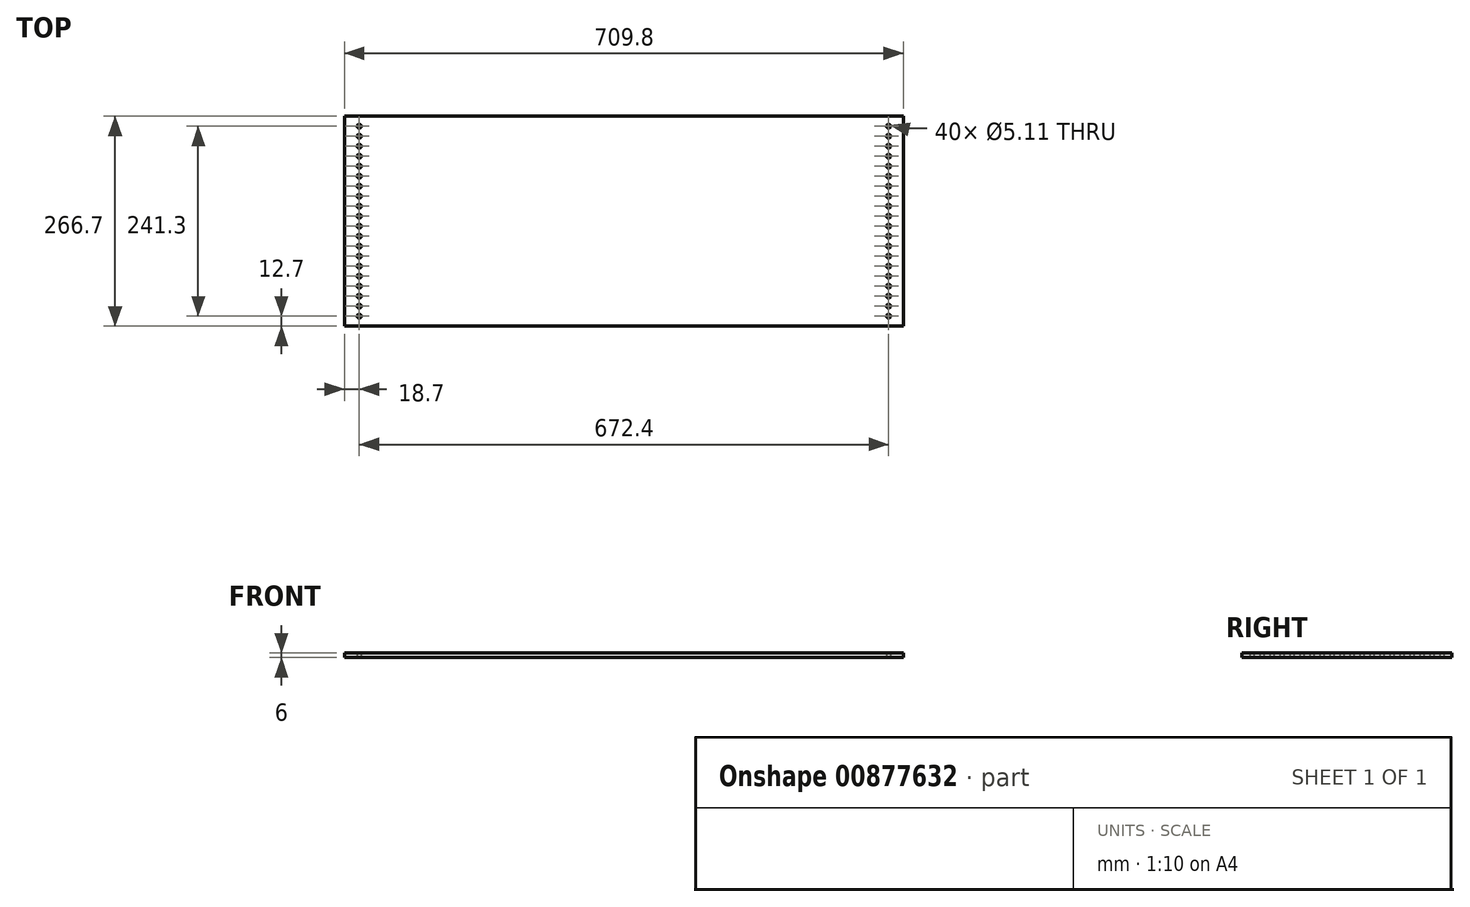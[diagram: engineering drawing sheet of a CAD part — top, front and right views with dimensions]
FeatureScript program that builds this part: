
annotation { "Feature Type Name" : "Feature", "Feature Type Description" : "" }
export const myFeature = defineFeature(function(context is Context, id is Id, definition is map)
    precondition{}
    {
        {
            var Q0;
            Q0=qCreatedBy(makeId("Top.planeOp"),FACE);
            var sketch = newSketch(context, id + "F0", { "sketchPlane" : qUnion([Q0])});
            skLineSegment(sketch, "E0.bottom", {"start": v(-354.9, 133.35) * mm, "end": v(354.9, 133.35) * mm});
            skLineSegment(sketch, "E0.top", {"start": v(-354.9, -133.35) * mm, "end": v(354.9, -133.35) * mm});
            skLineSegment(sketch, "E0.left", {"start": v(-354.9, 133.35) * mm, "end": v(-354.9, -133.35) * mm});
            skLineSegment(sketch, "E0.right", {"start": v(354.9, 133.35) * mm, "end": v(354.9, -133.35) * mm});
            skPoint(sketch, "E0.middle", {"position": v(0, 0) * mm});
            skCircle(sketch, "E1", {"center": v(-336.2, 120.65) * mm, "radius": 2.55 * mm});
            skCircle(sketch, "E2.0.1.0", {"center": v(-336.2, 107.95) * mm, "radius": 2.55 * mm});
            skCircle(sketch, "E2.0.2.0", {"center": v(-336.2, 95.25) * mm, "radius": 2.55 * mm});
            skCircle(sketch, "E2.0.3.0", {"center": v(-336.2, 82.55) * mm, "radius": 2.55 * mm});
            skCircle(sketch, "E2.0.4.0", {"center": v(-336.2, 69.85) * mm, "radius": 2.55 * mm});
            skCircle(sketch, "E2.0.5.0", {"center": v(-336.2, 57.15) * mm, "radius": 2.55 * mm});
            skCircle(sketch, "E2.0.6.0", {"center": v(-336.2, 44.45) * mm, "radius": 2.55 * mm});
            skCircle(sketch, "E2.0.7.0", {"center": v(-336.2, 31.75) * mm, "radius": 2.55 * mm});
            skCircle(sketch, "E2.0.8.0", {"center": v(-336.2, 19.05) * mm, "radius": 2.55 * mm});
            skCircle(sketch, "E2.0.9.0", {"center": v(-336.2, 6.35) * mm, "radius": 2.55 * mm});
            skCircle(sketch, "E2.0.10.0", {"center": v(-336.2, -6.35) * mm, "radius": 2.55 * mm});
            skCircle(sketch, "E2.0.11.0", {"center": v(-336.2, -19.05) * mm, "radius": 2.55 * mm});
            skCircle(sketch, "E2.0.12.0", {"center": v(-336.2, -31.75) * mm, "radius": 2.55 * mm});
            skCircle(sketch, "E2.0.13.0", {"center": v(-336.2, -44.45) * mm, "radius": 2.55 * mm});
            skCircle(sketch, "E2.0.14.0", {"center": v(-336.2, -57.15) * mm, "radius": 2.55 * mm});
            skCircle(sketch, "E2.0.15.0", {"center": v(-336.2, -69.85) * mm, "radius": 2.55 * mm});
            skCircle(sketch, "E2.0.16.0", {"center": v(-336.2, -82.55) * mm, "radius": 2.55 * mm});
            skCircle(sketch, "E2.0.17.0", {"center": v(-336.2, -95.25) * mm, "radius": 2.55 * mm});
            skCircle(sketch, "E2.0.18.0", {"center": v(-336.2, -107.95) * mm, "radius": 2.55 * mm});
            skCircle(sketch, "E2.0.19.0", {"center": v(-336.2, -120.65) * mm, "radius": 2.55 * mm});
            skLineSegment(sketch, "E2.direction1", {"start": v(-336.2, 120.65) * mm, "end": v(-285.4, 120.65) * mm, "construction": true});
            skLineSegment(sketch, "E2.direction2", {"start": v(-336.2, 120.65) * mm, "end": v(-336.2, 107.95) * mm, "construction": true});
            skCircle(sketch, "E3", {"center": v(336.2, 120.65) * mm, "radius": 2.55 * mm});
            skCircle(sketch, "E4.0.1.0", {"center": v(336.2, 107.95) * mm, "radius": 2.55 * mm});
            skCircle(sketch, "E4.0.2.0", {"center": v(336.2, 95.25) * mm, "radius": 2.55 * mm});
            skCircle(sketch, "E4.0.3.0", {"center": v(336.2, 82.55) * mm, "radius": 2.55 * mm});
            skCircle(sketch, "E4.0.4.0", {"center": v(336.2, 69.85) * mm, "radius": 2.55 * mm});
            skCircle(sketch, "E4.0.5.0", {"center": v(336.2, 57.15) * mm, "radius": 2.55 * mm});
            skCircle(sketch, "E4.0.6.0", {"center": v(336.2, 44.45) * mm, "radius": 2.55 * mm});
            skCircle(sketch, "E4.0.7.0", {"center": v(336.2, 31.75) * mm, "radius": 2.55 * mm});
            skCircle(sketch, "E4.0.8.0", {"center": v(336.2, 19.05) * mm, "radius": 2.55 * mm});
            skCircle(sketch, "E4.0.9.0", {"center": v(336.2, 6.35) * mm, "radius": 2.55 * mm});
            skCircle(sketch, "E4.0.10.0", {"center": v(336.2, -6.35) * mm, "radius": 2.55 * mm});
            skCircle(sketch, "E4.0.11.0", {"center": v(336.2, -19.05) * mm, "radius": 2.55 * mm});
            skCircle(sketch, "E4.0.12.0", {"center": v(336.2, -31.75) * mm, "radius": 2.55 * mm});
            skCircle(sketch, "E4.0.13.0", {"center": v(336.2, -44.45) * mm, "radius": 2.55 * mm});
            skCircle(sketch, "E4.0.14.0", {"center": v(336.2, -57.15) * mm, "radius": 2.55 * mm});
            skCircle(sketch, "E4.0.15.0", {"center": v(336.2, -69.85) * mm, "radius": 2.55 * mm});
            skCircle(sketch, "E4.0.16.0", {"center": v(336.2, -82.55) * mm, "radius": 2.55 * mm});
            skCircle(sketch, "E4.0.17.0", {"center": v(336.2, -95.25) * mm, "radius": 2.55 * mm});
            skCircle(sketch, "E4.0.18.0", {"center": v(336.2, -107.95) * mm, "radius": 2.55 * mm});
            skCircle(sketch, "E4.0.19.0", {"center": v(336.2, -120.65) * mm, "radius": 2.55 * mm});
            skLineSegment(sketch, "E4.direction1", {"start": v(336.2, 120.65) * mm, "end": v(336.2, 120.65) * mm});
            skLineSegment(sketch, "E4.direction2", {"start": v(336.2, 120.65) * mm, "end": v(336.2, 107.95) * mm, "construction": true});
            skSolve(sketch);
        }
        {
            var Q0;
            Q0=makeQuery(id+"F0.imprint","IMPRINT",FACE,{"disambiguationData":[TD([[makeQuery(id+"F0.imprint","IMPRINT",EDGE,{"derivedFrom":sQuery(id+"F0.wireOp",EDGE,"E0.bottom")}),-1.0]])]});
            extrude(context, id + "F1", {"entities" : qUnion([Q0]), "depth" : 6 * mm, "offsetDistance" : 25.4 * mm});
        }
    });
